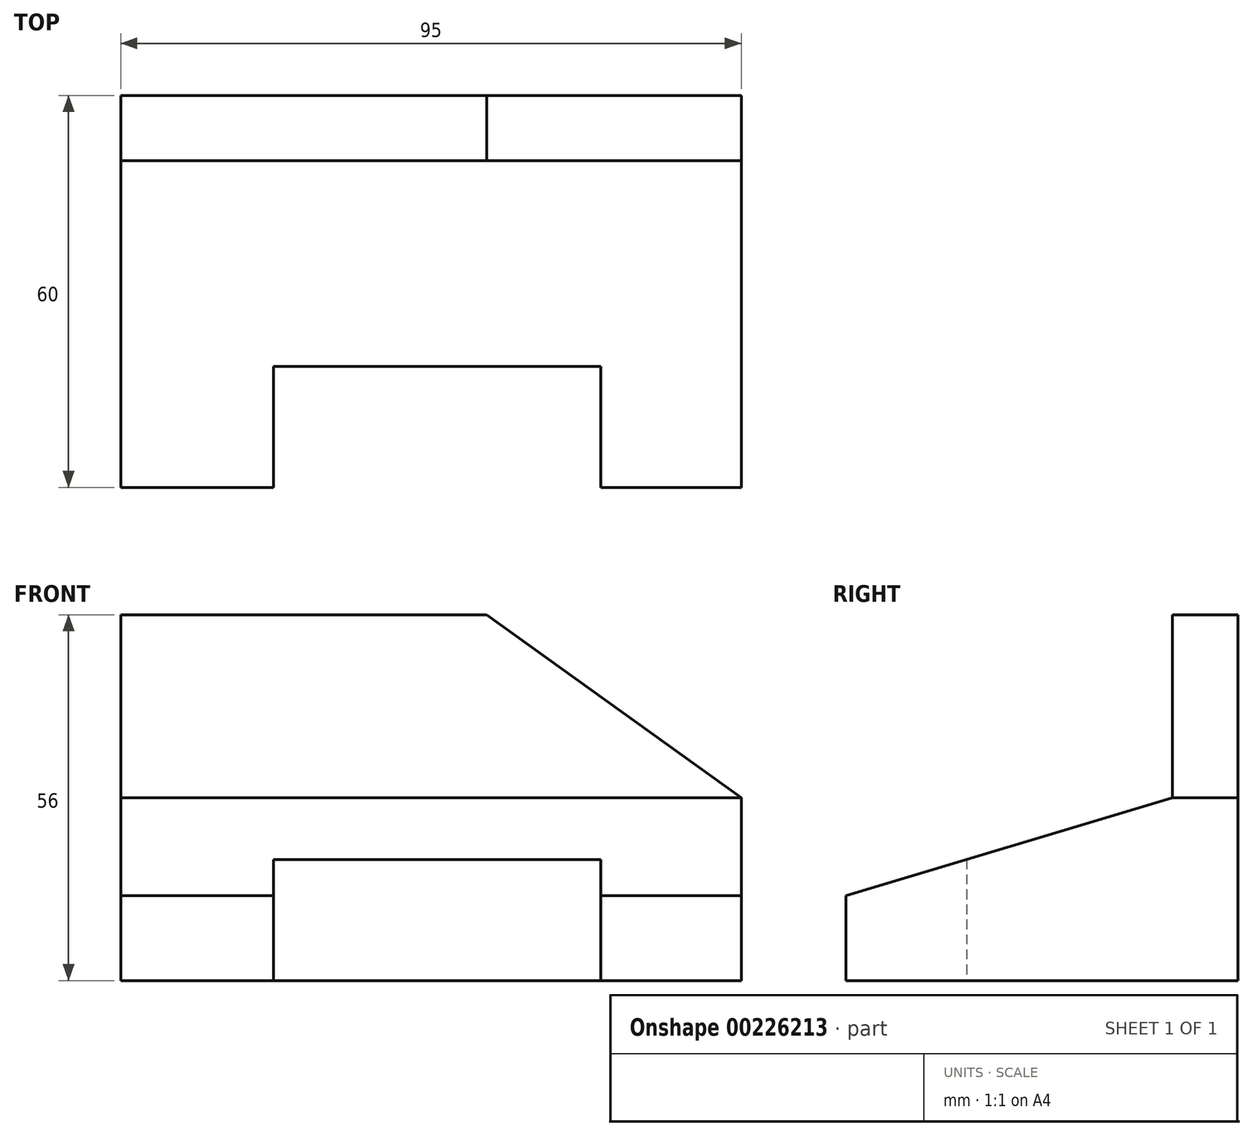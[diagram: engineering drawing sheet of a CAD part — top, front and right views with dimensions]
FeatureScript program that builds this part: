
annotation { "Feature Type Name" : "Feature", "Feature Type Description" : "" }
export const myFeature = defineFeature(function(context is Context, id is Id, definition is map)
    precondition{}
    {
        {
            var Q0;
            Q0=qCreatedBy(makeId("Right.planeOp"),FACE);
            var sketch = newSketch(context, id + "F0", { "sketchPlane" : qUnion([Q0])});
            skLineSegment(sketch, "E0", {"start": v(0, 0) * mm, "end": v(0, 56) * mm});
            skLineSegment(sketch, "E1", {"start": v(-10, 56) * mm, "end": v(-10, 28) * mm});
            skLineSegment(sketch, "E2", {"start": v(-10, 28) * mm, "end": v(-60, 13) * mm});
            skLineSegment(sketch, "E3", {"start": v(-60, 13) * mm, "end": v(-60, 0) * mm});
            skLineSegment(sketch, "E4", {"start": v(-60, 0) * mm, "end": v(0, 0) * mm});
            skLineSegment(sketch, "E5", {"start": v(0, 56) * mm, "end": v(-10, 56) * mm});
            skPoint(sketch, "E6", {"position": v(0, 28) * mm});
            skSolve(sketch);
        }
        {
            var Q0;
            Q0 = qSketchRegion(id + "F0", true);
            extrude(context, id + "F1", {"entities" : qUnion([Q0]), "depth" : 95 * mm});
        }
        {
            var Q0;
            Q0=makeQuery(id+"F1.opExtrude","SWEPT_FACE",FACE,{"disambiguationData":[OSD([sQuery(id+"F0.wireOp",EDGE,"E1")])]});
            var sketch = newSketch(context, id + "F2", { "sketchPlane" : qUnion([Q0])});
            skLineSegment(sketch, "E7", {"start": v(95, 28) * mm, "end": v(56, 56) * mm});
            skSolve(sketch);
        }
        {
            var Q0;
            {var subQ0=sQuery(id+"F2.wireOp",EDGE,"E7");Q0=makeQuery(id+"F2.imprint","IMPRINT",FACE,{"disambiguationData":[TD([[makeQuery(id+"F2.imprint","IMPRINT",EDGE,{"derivedFrom":subQ0}),-1.0]])]});}
            extrude(context, id + "F3", {"entities" : qUnion([Q0]), "operationType" : NewBodyOperationType.REMOVE, "oppositeDirection" : true, "depth" : 25 * mm});
        }
        {
            var Q0;
            Q0=makeQuery(id+"F1.opExtrude","SWEPT_FACE",FACE,{"disambiguationData":[OSD([sQuery(id+"F0.wireOp",EDGE,"E4")])]});
            var sketch = newSketch(context, id + "F4", { "sketchPlane" : qUnion([Q0])});
            skLineSegment(sketch, "E8.bottom", {"start": v(23.38, 60) * mm, "end": v(73.46, 60) * mm});
            skLineSegment(sketch, "E8.top", {"start": v(23.38, 41.51) * mm, "end": v(73.46, 41.51) * mm});
            skLineSegment(sketch, "E8.left", {"start": v(23.38, 60) * mm, "end": v(23.38, 41.51) * mm});
            skLineSegment(sketch, "E8.right", {"start": v(73.46, 60) * mm, "end": v(73.46, 41.51) * mm});
            skSolve(sketch);
        }
        {
            var Q0;
            Q0=makeQuery(id+"F4.imprint","IMPRINT",FACE,{"disambiguationData":[TD([[makeQuery(id+"F4.imprint","IMPRINT",EDGE,{"derivedFrom":sQuery(id+"F4.wireOp",EDGE,"E8.bottom")}),1.0]])]});
            extrude(context, id + "F5", {"entities" : qUnion([Q0]), "operationType" : NewBodyOperationType.REMOVE, "endBound" : BoundingType.THROUGH_ALL, "oppositeDirection" : true, "depth" : 25 * mm});
        }
    });
